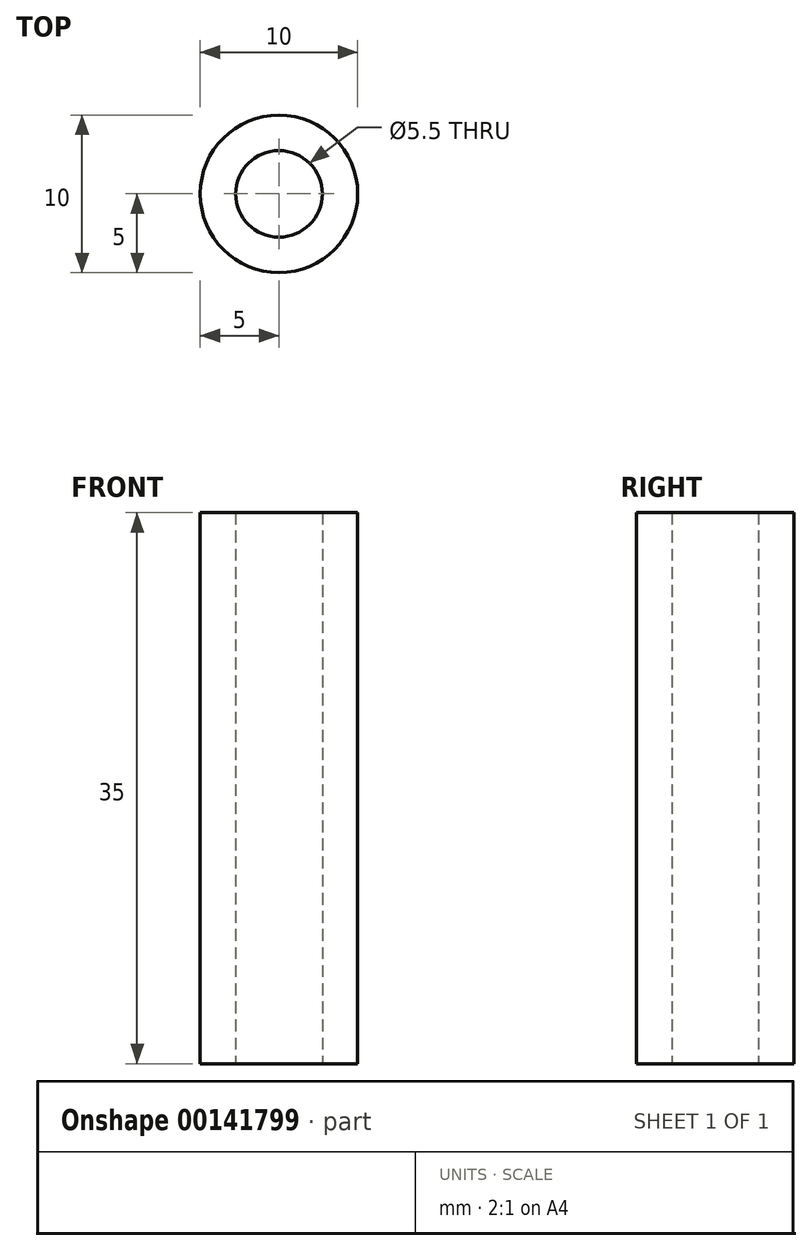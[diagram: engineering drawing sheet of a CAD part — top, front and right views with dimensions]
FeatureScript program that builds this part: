
annotation { "Feature Type Name" : "Feature", "Feature Type Description" : "" }
export const myFeature = defineFeature(function(context is Context, id is Id, definition is map)
    precondition{}
    {
        {
            var Q0;
            Q0=qCreatedBy(makeId("Top.planeOp"),FACE);
            var sketch = newSketch(context, id + "F0", { "sketchPlane" : qUnion([Q0])});
            skLineSegment(sketch, "E0", {"start": v(-18.5, 0) * mm, "end": v(18.5, 0) * mm, "construction": true});
            skCircle(sketch, "E1", {"center": v(-15.75, 0) * mm, "radius": 2.75 * mm});
            skCircle(sketch, "E2", {"center": v(15.75, 0) * mm, "radius": 2.75 * mm});
            skCircle(sketch, "E3", {"center": v(-15.75, 0) * mm, "radius": 5 * mm});
            skCircle(sketch, "E4", {"center": v(15.75, 0) * mm, "radius": 5 * mm});
            skLineSegment(sketch, "E5", {"start": v(0, -10) * mm, "end": v(0, 0) * mm, "construction": true});
            skLineSegment(sketch, "E6", {"start": v(0, -10) * mm, "end": v(-17.2, -4.78) * mm});
            skLineSegment(sketch, "E7", {"start": v(0, -10) * mm, "end": v(17.2, -4.78) * mm});
            skLineSegment(sketch, "E8", {"start": v(0, 0) * mm, "end": v(-14.16, 4.74) * mm});
            skLineSegment(sketch, "E9", {"start": v(0, 0) * mm, "end": v(14.16, 4.74) * mm});
            skSolve(sketch);
        }
        {
            var Q0;
            Q0=makeQuery(id+"F0.imprint","IMPRINT",FACE,{"disambiguationData":[TD([[makeQuery(id+"F0.imprint","IMPRINT",EDGE,{"derivedFrom":sQuery(id+"F0.wireOp",EDGE,"E1")}),-1.0]])]});
            extrude(context, id + "F1", {"entities" : qUnion([Q0]), "depth" : 35 * mm});
        }
    });
